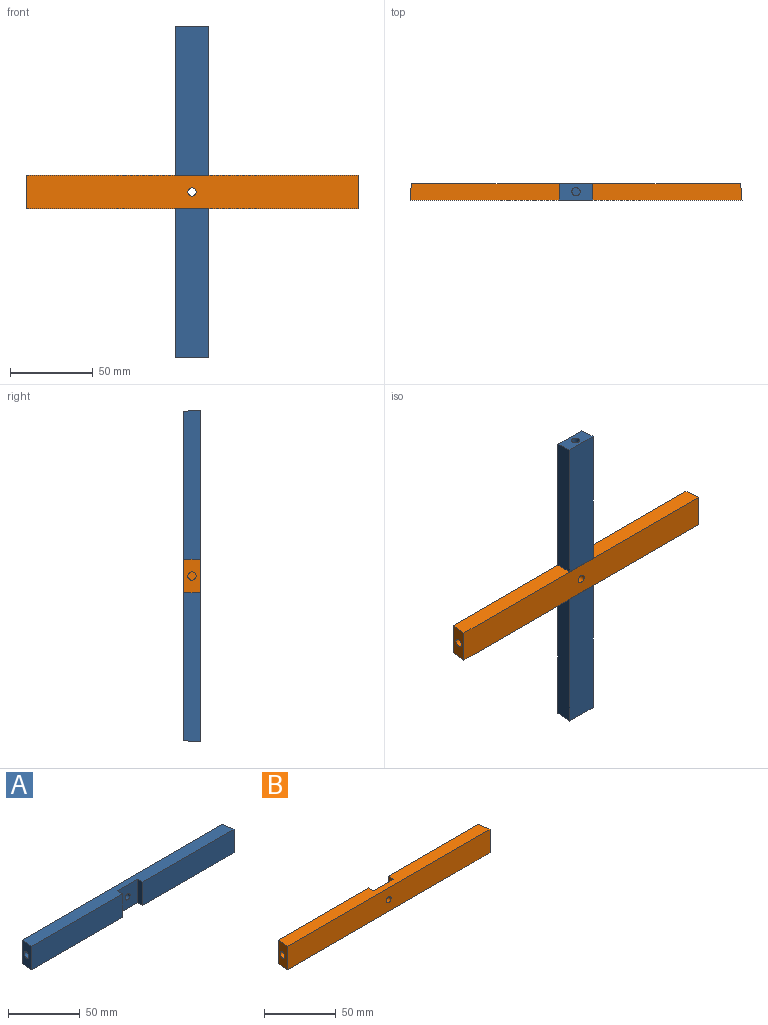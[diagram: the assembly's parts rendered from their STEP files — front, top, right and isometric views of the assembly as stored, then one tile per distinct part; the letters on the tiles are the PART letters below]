
ASSEMBLY  parts=2 mates=1
PART A: 15 faces, bbox 200.1x10.1x20.1 mm
  f0: plane 200x10mm, normal (0,0,1), area 1891.3mm2, adj f1,f3,f4,f5,f6,f7,f8,f9
  f1: plane 198.25x20mm, normal (0,1,0), area 3945.4mm2, adj f0,f2,f8,f9,f14
  f2: plane 200x10mm, normal (0,0,-1), area 1891.3mm2, adj f1,f3,f4,f5,f6,f7,f8,f9
  f3: plane 90x20mm, normal (0,-1,0), area 1800mm2, adj f0,f2,f6,f8
  f4: plane 90x20mm, normal (0,-1,0), area 1800mm2, adj f0,f2,f5,f9
  f5: plane 20x5mm, normal (1,0,0), area 100mm2, adj f0,f2,f4,f7
  f6: plane 20x5mm, normal (-1,0,0), area 100mm2, adj f0,f2,f3,f7
  f7: plane 20x20mm, normal (0,-1,0), area 380.4mm2, adj f0,f2,f5,f6,f14
  f8: plane 20.09x10.09mm, normal (1,0.09,0), area 181.1mm2, adj f0,f1,f2,f3,f11
  f9: plane 20.09x10.09mm, normal (-1,0.09,0), area 181.1mm2, adj f0,f1,f2,f4,f13
  f10: plane 5x5mm, normal (1,0,0), area 19.6mm2, adj f11
  f11: cylinder r=2.5mm len=5mm, axis (1,0,0), area 71.6mm2, adj f8,f10
  f12: plane 5x5mm, normal (-1,0,0), area 19.6mm2, adj f13
  f13: cylinder r=2.5mm len=5mm, axis (-1,0,0), area 71.6mm2, adj f9,f12
  f14: cylinder r=2.5mm len=5mm, axis (0,-1,0), area 78.5mm2, adj f1,f7
PART B: 15 faces, bbox 200.1x10.1x20.1 mm
  f0: plane 89.13x20mm, normal (0,1,0), area 1782.5mm2, adj f1,f5,f8,f11
  f1: plane 200x10mm, normal (0,0,1), area 1891.3mm2, adj f0,f4,f6,f7,f8,f11,f12,f13
  f2: cylinder r=2.5mm len=5mm, axis (-1,0,0), area 71.6mm2, adj f3,f4
  f3: plane 5x5mm, normal (-1,0,0), area 19.6mm2, adj f2
  f4: plane 20.09x10.09mm, normal (-1,0.09,0), area 181.1mm2, adj f1,f2,f5,f6,f7
  f5: plane 200x10mm, normal (0,0,-1), area 1891.3mm2, adj f0,f4,f6,f7,f8,f11,f12,f13
  f6: plane 89.13x20mm, normal (0,1,0), area 1782.5mm2, adj f1,f4,f5,f12
  f7: plane 200x20mm, normal (0,-1,0), area 3980.4mm2, adj f1,f4,f5,f8,f14
  f8: plane 20.09x10.09mm, normal (1,0.09,0), area 181.1mm2, adj f0,f1,f5,f7,f10
  f9: plane 5x5mm, normal (1,0,0), area 19.6mm2, adj f10
  f10: cylinder r=2.5mm len=5mm, axis (1,0,0), area 71.6mm2, adj f8,f9
  f11: plane 20x5mm, normal (-1,0,0), area 100mm2, adj f0,f1,f5,f13
  f12: plane 20x5mm, normal (1,0,0), area 100mm2, adj f1,f5,f6,f13
  f13: plane 20x20mm, normal (0,1,0), area 380.4mm2, adj f1,f5,f11,f12,f14
  f14: cylinder r=2.5mm len=5mm, axis (0,1,0), area 78.5mm2, adj f7,f13
PLACE A rot(axis=(0,-1,0),90deg) t=(4.2,-87.37,39.53)mm
PLACE B t=(4.2,-87.37,39.53)mm
MATE fastened B.f14 <-> A.f14  axis (0,1,0) through (4.2,-92.37,39.53)mm
